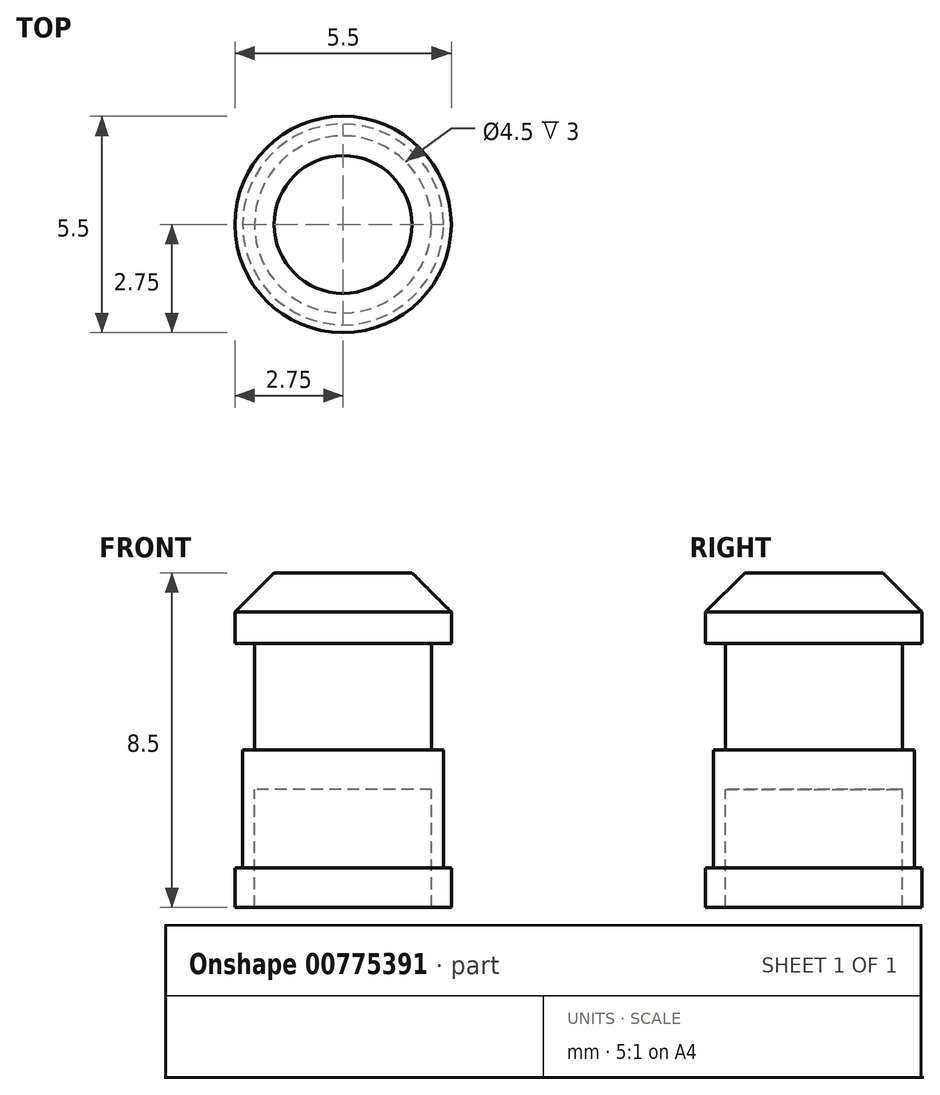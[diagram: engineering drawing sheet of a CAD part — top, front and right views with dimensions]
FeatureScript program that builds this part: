
annotation { "Feature Type Name" : "Feature", "Feature Type Description" : "" }
export const myFeature = defineFeature(function(context is Context, id is Id, definition is map)
    precondition{}
    {
        {
            var Q0;
            Q0=qCreatedBy(makeId("Top.planeOp"),FACE);
            var sketch = newSketch(context, id + "F0", { "sketchPlane" : qUnion([Q0])});
            skCircle(sketch, "E0", {"center": v(0, 0) * mm, "radius": 2.55 * mm});
            skCircle(sketch, "E1", {"center": v(0, 0) * mm, "radius": 2.25 * mm});
            skCircle(sketch, "E2", {"center": v(0, 0) * mm, "radius": 3 * mm});
            skCircle(sketch, "E3", {"center": v(0, 0) * mm, "radius": 2.75 * mm});
            skSolve(sketch);
        }
        {
            var Q0;
            Q0=makeQuery(id+"F0.imprint","IMPRINT",FACE,{"disambiguationData":[TD([[makeQuery(id+"F0.imprint","IMPRINT",EDGE,{"derivedFrom":sQuery(id+"F0.wireOp",EDGE,"E0")}),1.0]])]});
            extrude(context, id + "F1", {"entities" : qUnion([Q0]), "oppositeDirection" : true, "depth" : 4 * mm, "offsetDistance" : 25 * mm});
        }
        {
            var Q0;
            Q0=makeQuery(id+"F0.imprint","IMPRINT",FACE,{"disambiguationData":[TD([[makeQuery(id+"F0.imprint","IMPRINT",EDGE,{"derivedFrom":sQuery(id+"F0.wireOp",EDGE,"E0")}),-1.0]])]});
            extrude(context, id + "F2", {"entities" : qUnion([Q0]), "operationType" : NewBodyOperationType.ADD, "oppositeDirection" : true, "depth" : 4 * mm, "offsetDistance" : 25 * mm, "hasSecondDirection" : true, "secondDirectionOppositeDirection" : true, "secondDirectionDepth" : 3 * mm});
        }
        {
            var Q0;
            Q0=makeQuery(id+"F0.imprint","IMPRINT",FACE,{"disambiguationData":[TD([[makeQuery(id+"F0.imprint","IMPRINT",EDGE,{"derivedFrom":sQuery(id+"F0.wireOp",EDGE,"E1")}),1.0]])]});
            extrude(context, id + "F3", {"entities" : qUnion([Q0]), "operationType" : NewBodyOperationType.ADD, "depth" : 4.5 * mm, "offsetDistance" : 25 * mm, "hasSecondDirection" : true, "secondDirectionOppositeDirection" : true, "secondDirectionDepth" : 1 * mm});
        }
        {
            var Q0;
            Q0=makeQuery(id+"F0.imprint","IMPRINT",FACE,{"disambiguationData":[TD([[makeQuery(id+"F0.imprint","IMPRINT",EDGE,{"derivedFrom":sQuery(id+"F0.wireOp",EDGE,"E0")}),1.0]])]});
            var Q1;
            Q1=makeQuery(id+"F0.imprint","IMPRINT",FACE,{"disambiguationData":[TD([[makeQuery(id+"F0.imprint","IMPRINT",EDGE,{"derivedFrom":sQuery(id+"F0.wireOp",EDGE,"E0")}),-1.0]])]});
            var Q2;
            Q2=sQuery(id+"F0.wireOp",EDGE,"E0");
            var Q3;
            Q3=sQuery(id+"F0.wireOp",EDGE,"E1");
            extrude(context, id + "F4", {"entities" : qUnion([Q0, Q1]), "operationType" : NewBodyOperationType.ADD, "surfaceEntities" : qUnion([Q2, Q3]), "depth" : 4.5 * mm, "offsetDistance" : 25 * mm, "hasSecondDirection" : true, "secondDirectionOppositeDirection" : false, "secondDirectionDepth" : 2.7 * mm});
        }
        {
            var Q0;
            {var subQ0=sQuery(id+"F0.wireOp",EDGE,"E1");Q0=makeQuery(id+"F4.boolean.opBoolean","MERGE",FACE,{"derivedFrom":[makeQuery(id+"F3.opExtrude","CAP_FACE",FACE,{"disambiguationData":[OSD([subQ0])],"isStart":false}),makeQuery(id+"F4.opExtrude","CAP_FACE",FACE,{"disambiguationData":[OSD([sQuery(id+"F0.wireOp",EDGE,"E0"),subQ0])],"isStart":false})]});}
            var Q1;
            Q1=makeQuery(id+"F2.opExtrude","CAP_EDGE",EDGE,{"disambiguationData":[OSD([sQuery(id+"F0.wireOp",EDGE,"E2")])],"isStart":false});
            chamfer(context, id + "F5", {"entities" : qUnion([Q0, Q1]), "width" : 1 * mm, "tangentPropagation" : true});
        }
    });
